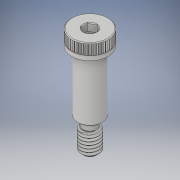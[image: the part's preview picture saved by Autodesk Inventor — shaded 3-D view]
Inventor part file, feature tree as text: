
AUTODESK INVENTOR PART (.ipt)
format: ipt  version: 2017 (Build 210142000, 142)  size: 594,432 bytes
history: native  units: in
note: dims shown in document units (in); Inventor stores cm internally (conversion verified against a paired STEP export)
features: chamfer x1
ambient origin geometry x8: Origin, YZ Plane, XZ Plane, XY Plane, X Axis, Y Axis, Z Axis, Center Point
bodies: Solid1 (feature_tree)
feature tree (1):
  chamfer  "Chamfer3"  [1 undecoded]
note: 1 required parameter value undecoded (feature->parameter linkage not recoverable at this tier; creation-order binding heuristic only, values carry confidence <= 0.55)
